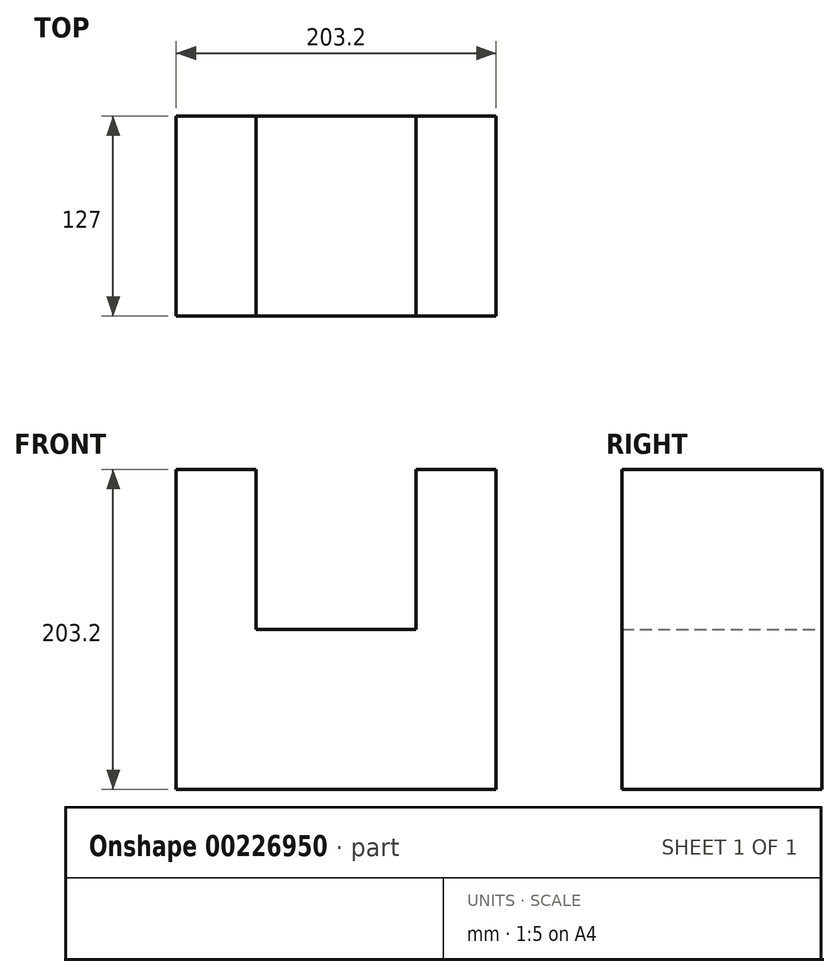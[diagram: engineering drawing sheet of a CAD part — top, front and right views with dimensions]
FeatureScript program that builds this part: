
annotation { "Feature Type Name" : "Feature", "Feature Type Description" : "" }
export const myFeature = defineFeature(function(context is Context, id is Id, definition is map)
    precondition{}
    {
        {
            var Q0;
            Q0=qCreatedBy(makeId("Front.planeOp"),FACE);
            var sketch = newSketch(context, id + "F0", { "sketchPlane" : qUnion([Q0])});
            skLineSegment(sketch, "E0.top", {"start": v(-121.54, -137.17) * mm, "end": v(81.66, -137.17) * mm});
            skLineSegment(sketch, "E0.left", {"start": v(-121.54, 66.03) * mm, "end": v(-121.54, -137.17) * mm});
            skLineSegment(sketch, "E0.right", {"start": v(81.66, 66.03) * mm, "end": v(81.66, -137.17) * mm});
            skLineSegment(sketch, "E1", {"start": v(-70.74, 66.03) * mm, "end": v(-70.74, -35.57) * mm});
            skLineSegment(sketch, "E2", {"start": v(-70.74, -35.57) * mm, "end": v(30.86, -35.57) * mm});
            skLineSegment(sketch, "E3", {"start": v(30.86, -35.57) * mm, "end": v(30.86, 66.03) * mm});
            skLineSegment(sketch, "E4", {"start": v(-121.54, 66.03) * mm, "end": v(-70.74, 66.03) * mm});
            skLineSegment(sketch, "E5", {"start": v(30.86, 66.03) * mm, "end": v(81.66, 66.03) * mm});
            skSolve(sketch);
        }
        {
            var Q0;
            Q0 = qSketchRegion(id + "F0", true);
            extrude(context, id + "F1", {"entities" : qUnion([Q0]), "depth" : 127 * mm});
        }
    });
